# Revit family: FH2 - 4300 bis 9300 plus
name_source: partatom
category: HLS-Bauteile
revit_build: Autodesk Revit 2017 (Build: 20190507_1515(x64)
units: mm (PartAtom-declared; Revit-internal decimal feet)

## family parameters
Arbeitsebenenbasiert = Ja
Beim Laden mit Abzugskörper schneiden = Nein
Bemaßung runder Anschluss = Durchmesser verwenden
Gemeinsam genutzt = Ja
Immer vertikal = Nein
Raumberechnungspunkt = Nein
Teiletyp = Normal

## types (3) — shared parameters
Anschluss = M16
Breite = 80 mm  [stored 0.262467 ft]
Fabrikat = MEFA
Firma = MEFA Befestigungs- und Montagesysteme GmbH
Höhe = 140 mm
Länge = 140 mm  [stored 0.459318 ft]
Material = Stahl
Materialname = S235
Mengeneinheit = St
Oberflaeche = galvanisch verzinkt
Vorgabe-Ansicht = 1219 mm
vpe = 1 St

## per-type parameters (varying)
| type | Artikelnummer | EAN | Federrate | Gewicht | Gewicht pro Bauteil | Kurztext2 | max. Federweg | max. Lastbereich | min. Lastbereich |
| Federhänger FH 2 - 4300 plus | 079170430 | 4250928449191 | 150,92 N/mm | 5.09 kg | 5.09 kg | F 0 - 4.301 N max. Federweg 29 mm | 29 mm  [stored 0.0951444 ft] | 4.301 N | 0 N |
| Federhänger FH 2 - 6000 plus | 079170600 | 4250928449207 | 268,6 N/mm | 5.11 kg | 5.11 kg | F 0 - 6.044 N max. Federweg 23 mm | 23 mm  [stored 0.0754593 ft] | 6.044 N | 0 N |
| Federhänger FH 2 - 9300 plus | 079180930 | 4250928449214 | 477,28 N/mm | 5.13 kg | 5.13 kg | F 2386 - 9.545 N max. Federweg 15 mm | 15 mm  [stored 0.0492126 ft] | 9.545 N | 2.386 N |

note: column(s) folded — value = type name in every type: Kurztext1

note: [stored X ft] marks values corroborated as IEEE doubles in the binary element streams (Revit-internal decimal feet)
